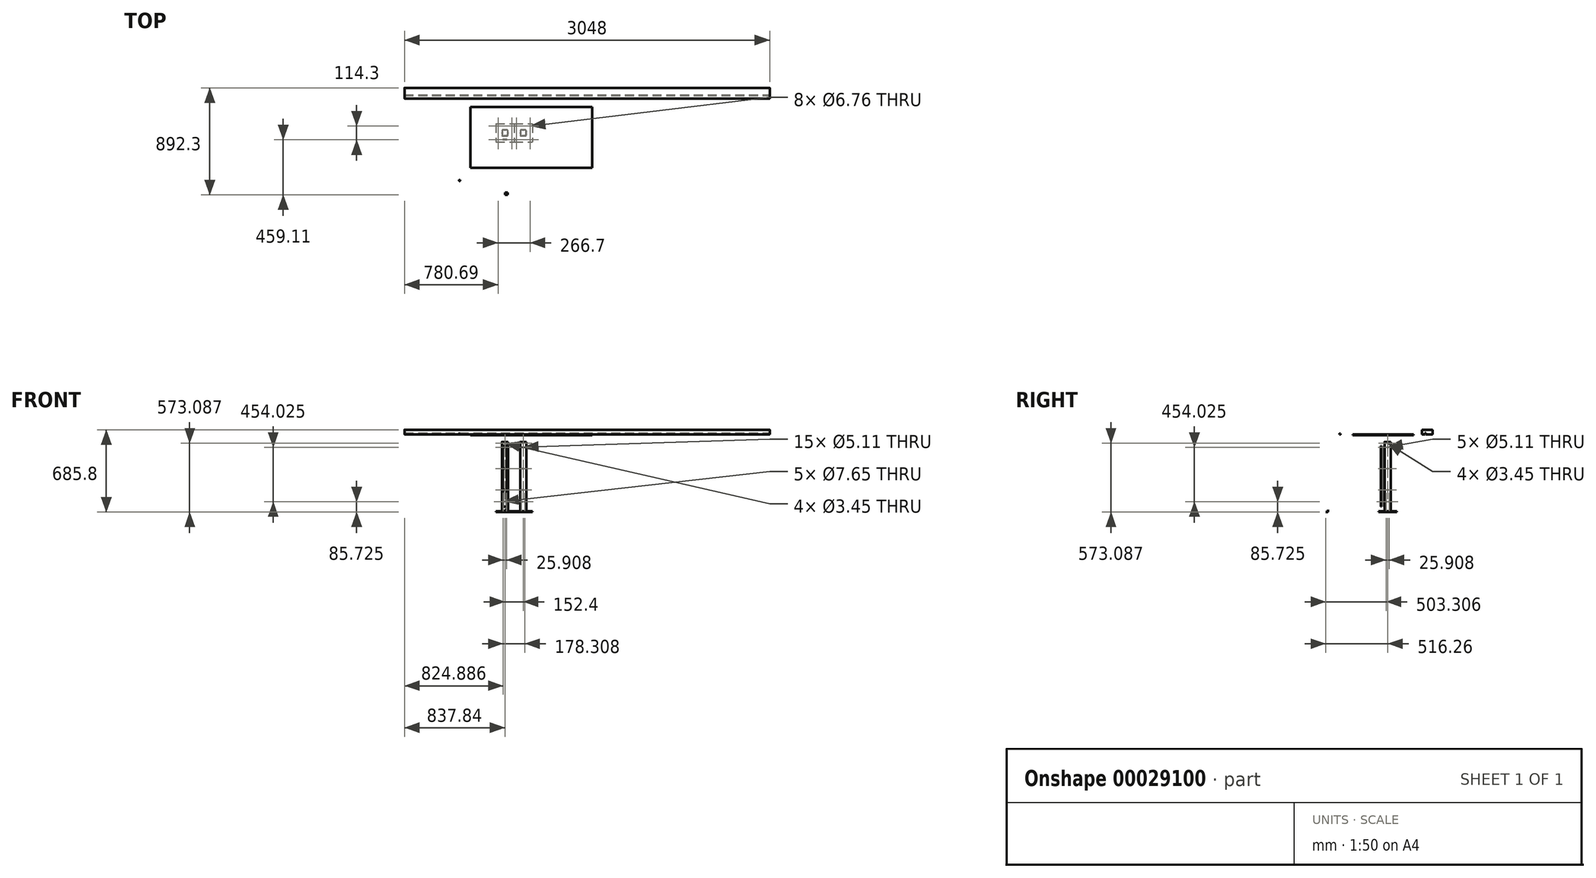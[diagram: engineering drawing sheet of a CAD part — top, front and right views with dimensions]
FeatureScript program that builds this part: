
annotation { "Feature Type Name" : "Feature", "Feature Type Description" : "" }
export const myFeature = defineFeature(function(context is Context, id is Id, definition is map)
    precondition{}
    {
        {
            var Q0;
            Q0=qCreatedBy(makeId("Top.planeOp"),FACE);
            var sketch = newSketch(context, id + "F0", { "sketchPlane" : qUnion([Q0])});
            skLineSegment(sketch, "E0.bottom", {"start": v(-76.2, 76.2) * mm, "end": v(76.2, 76.2) * mm});
            skLineSegment(sketch, "E0.top", {"start": v(-76.2, -76.2) * mm, "end": v(76.2, -76.2) * mm});
            skLineSegment(sketch, "E0.left", {"start": v(-76.2, 76.2) * mm, "end": v(-76.2, -76.2) * mm});
            skLineSegment(sketch, "E0.right", {"start": v(76.2, 76.2) * mm, "end": v(76.2, -76.2) * mm});
            skSolve(sketch);
        }
        {
            var Q0;
            Q0 = qSketchRegion(id + "F0", true);
            extrude(context, id + "F1", {"entities" : qUnion([Q0]), "depth" : 6.35 * mm});
        }
        {
            var Q0;
            Q0=makeQuery(id+"F1.opExtrude","CAP_FACE",FACE,{"disambiguationData":[OSD([sQuery(id+"F0.wireOp",EDGE,"E0.bottom"),sQuery(id+"F0.wireOp",EDGE,"E0.top"),sQuery(id+"F0.wireOp",EDGE,"E0.left"),sQuery(id+"F0.wireOp",EDGE,"E0.right")])],"isStart":false});
            var sketch = newSketch(context, id + "F2", { "sketchPlane" : qUnion([Q0])});
            skLineSegment(sketch, "E1.0", {"start": v(19.3, 25.4) * mm, "end": v(-19.3, 25.4) * mm});
            skLineSegment(sketch, "E1.1", {"start": v(25.4, -19.3) * mm, "end": v(25.4, 19.3) * mm});
            skLineSegment(sketch, "E1.2", {"start": v(-19.3, -25.4) * mm, "end": v(19.3, -25.4) * mm});
            skLineSegment(sketch, "E1.3", {"start": v(-25.4, 19.3) * mm, "end": v(-25.4, -19.3) * mm});
            skLineSegment(sketch, "E2.0", {"start": v(-22.35, 19.3) * mm, "end": v(-22.35, -19.18) * mm});
            skLineSegment(sketch, "E2.1", {"start": v(19.3, 22.35) * mm, "end": v(-19.3, 22.35) * mm});
            skLineSegment(sketch, "E2.2", {"start": v(22.35, -19.3) * mm, "end": v(22.35, 19.3) * mm});
            skLineSegment(sketch, "E2.3", {"start": v(-19.18, -22.35) * mm, "end": v(19.3, -22.35) * mm});
            skPoint(sketch, "E3.visualSharp", {"position": v(-22.35, -22.35) * mm});
            skArc(sketch, "E3.filletArc", {"start": v(-22.35, -19.18) * mm, "mid": v(-21.42, -21.42) * mm, "end": v(-19.18, -22.35) * mm});
            skPoint(sketch, "E4.visualSharp", {"position": v(-25.4, -25.4) * mm});
            skArc(sketch, "E4.filletArc", {"start": v(-25.4, -19.3) * mm, "mid": v(-23.61, -23.61) * mm, "end": v(-19.3, -25.4) * mm});
            skPoint(sketch, "E5.visualSharp", {"position": v(22.35, -22.35) * mm});
            skArc(sketch, "E5.filletArc", {"start": v(19.3, -22.35) * mm, "mid": v(21.46, -21.46) * mm, "end": v(22.35, -19.3) * mm});
            skPoint(sketch, "E6.visualSharp", {"position": v(25.4, -25.4) * mm});
            skArc(sketch, "E6.filletArc", {"start": v(19.3, -25.4) * mm, "mid": v(23.61, -23.61) * mm, "end": v(25.4, -19.3) * mm});
            skPoint(sketch, "E7.visualSharp", {"position": v(22.35, 22.35) * mm});
            skArc(sketch, "E7.filletArc", {"start": v(22.35, 19.3) * mm, "mid": v(21.46, 21.46) * mm, "end": v(19.3, 22.35) * mm});
            skPoint(sketch, "E8.visualSharp", {"position": v(25.4, 25.4) * mm});
            skArc(sketch, "E8.filletArc", {"start": v(25.4, 19.3) * mm, "mid": v(23.61, 23.61) * mm, "end": v(19.3, 25.4) * mm});
            skPoint(sketch, "E9.visualSharp", {"position": v(-22.35, 22.35) * mm});
            skArc(sketch, "E9.filletArc", {"start": v(-19.3, 22.35) * mm, "mid": v(-21.46, 21.46) * mm, "end": v(-22.35, 19.3) * mm});
            skPoint(sketch, "E10.visualSharp", {"position": v(-25.4, 25.4) * mm});
            skArc(sketch, "E10.filletArc", {"start": v(-19.3, 25.4) * mm, "mid": v(-23.61, 23.61) * mm, "end": v(-25.4, 19.3) * mm});
            skSolve(sketch);
        }
        {
            var Q0;
            Q0 = qSketchRegion(id + "F2", true);
            extrude(context, id + "F3", {"entities" : qUnion([Q0]), "operationType" : NewBodyOperationType.ADD, "depth" : 577.85 * mm});
        }
        {
            var Q0;
            Q0=makeQuery(id+"F3.opExtrude","SWEPT_FACE",FACE,{"disambiguationData":[OSD([sQuery(id+"F2.wireOp",EDGE,"E1.2")])]});
            var sketch = newSketch(context, id + "F4", { "sketchPlane" : qUnion([Q0])});
            skPoint(sketch, "E11", {"position": v(12.95, 85.72) * mm});
            skPoint(sketch, "E12", {"position": v(-12.95, 85.72) * mm});
            skPoint(sketch, "E13", {"position": v(0, 539.75) * mm});
            skPoint(sketch, "E14", {"position": v(0, 361.95) * mm});
            skPoint(sketch, "E15", {"position": v(0, 184.15) * mm});
            skPoint(sketch, "E16", {"position": v(0, 573.09) * mm});
            skSolve(sketch);
        }
        {
            var Q0;
            Q0=sQuery(id+"F4.wireOp",VERTEX,"E12");
            var Q1;
            Q1=sQuery(id+"F4.wireOp",VERTEX,"E11");
            var Q2;
            Q2=sQuery(id+"F4.wireOp",VERTEX,"E15");
            var Q3;
            Q3=sQuery(id+"F4.wireOp",VERTEX,"E14");
            var Q4;
            Q4=sQuery(id+"F4.wireOp",VERTEX,"E13");
            var Q5;
            Q5=makeQuery(id+"F1.opExtrude","SWEPT_BODY",BODY,{"disambiguationData":[OSD([sQuery(id+"F0.wireOp",EDGE,"E0.bottom"),sQuery(id+"F0.wireOp",EDGE,"E0.top"),sQuery(id+"F0.wireOp",EDGE,"E0.left"),sQuery(id+"F0.wireOp",EDGE,"E0.right")])]});
            hole(context, id + "F5", {"style" : HoleStyle.SIMPLE, "endStyle" : HoleEndStyle.BLIND, "standardTappedOrClearance" : lookupTablePath({ "standard" : "ANSI", "engagement" : "75%", "pitch" : "20 tpi", "size" : "1/4", "type" : "Tapped" }), "standardBlindInLast" : lookupTablePath({ "standard" : "ANSI", "engagement" : "75%", "pitch" : "20 tpi", "size" : "1/4", "type" : "Tapped" }), "holeDiameter" : 5.1 * mm, "holeDepth" : 12.7 * mm, "locations" : qUnion([Q0, Q1, Q2, Q3, Q4]), "scope" : qUnion([Q5]), "majorDiameter" : 6.35 * mm});
        }
        {
            var Q0;
            Q0=sQuery(id+"F4.wireOp",VERTEX,"E16");
            var Q1;
            Q1=makeQuery(id+"F1.opExtrude","SWEPT_BODY",BODY,{"disambiguationData":[OSD([sQuery(id+"F0.wireOp",EDGE,"E0.bottom"),sQuery(id+"F0.wireOp",EDGE,"E0.top"),sQuery(id+"F0.wireOp",EDGE,"E0.left"),sQuery(id+"F0.wireOp",EDGE,"E0.right")])]});
            hole(context, id + "F6", {"style" : HoleStyle.SIMPLE, "endStyle" : HoleEndStyle.THROUGH, "standardTappedOrClearance" : lookupTablePath({ "standard" : "ANSI", "engagement" : "75%", "pitch" : "32 tpi", "size" : "#8", "type" : "Tapped" }), "standardBlindInLast" : lookupTablePath({ "standard" : "ANSI", "engagement" : "75%", "pitch" : "32 tpi", "size" : "#8", "type" : "Tapped" }), "holeDiameter" : 3.45 * mm, "startFromSketch" : true, "locations" : qUnion([Q0]), "scope" : qUnion([Q1]), "isTappedThrough" : true, "majorDiameter" : 4.17 * mm, "showTappedDepth" : true});
        }
        {
            var Q0;
            {var subQ0=sQuery(id+"F0.wireOp",EDGE,"E0.left");var subQ1=sQuery(id+"F0.wireOp",EDGE,"E0.bottom");var subQ2=sQuery(id+"F0.wireOp",EDGE,"E0.top");var subQ3=sQuery(id+"F0.wireOp",EDGE,"E0.right");Q0=makeQuery(id+"F3.boolean.opBoolean","SPLIT",FACE,{"disambiguationData":[TD([makeQuery(id+"F1.opExtrude","SWEPT_FACE",FACE,{"disambiguationData":[OSD([subQ1])]})])],"derivedFrom":makeQuery(id+"F1.opExtrude","CAP_FACE",FACE,{"disambiguationData":[OSD([subQ1,subQ2,subQ0,subQ3])],"isStart":false})});}
            var sketch = newSketch(context, id + "F7", { "sketchPlane" : qUnion([Q0])});
            skPoint(sketch, "E17", {"position": v(-57.15, 57.15) * mm});
            skPoint(sketch, "E18", {"position": v(-57.15, -57.15) * mm});
            skPoint(sketch, "E19", {"position": v(57.15, -57.15) * mm});
            skPoint(sketch, "E20", {"position": v(57.15, 57.15) * mm});
            skSolve(sketch);
        }
        {
            var Q0;
            Q0=sQuery(id+"F7.wireOp",VERTEX,"E17");
            var Q1;
            Q1=sQuery(id+"F7.wireOp",VERTEX,"E18");
            var Q2;
            Q2=sQuery(id+"F7.wireOp",VERTEX,"E19");
            var Q3;
            Q3=sQuery(id+"F7.wireOp",VERTEX,"E20");
            var Q4;
            Q4=makeQuery(id+"F1.opExtrude","SWEPT_BODY",BODY,{"disambiguationData":[OSD([sQuery(id+"F0.wireOp",EDGE,"E0.bottom"),sQuery(id+"F0.wireOp",EDGE,"E0.top"),sQuery(id+"F0.wireOp",EDGE,"E0.left"),sQuery(id+"F0.wireOp",EDGE,"E0.right")])]});
            hole(context, id + "F8", {"style" : HoleStyle.SIMPLE, "endStyle" : HoleEndStyle.THROUGH, "standardTappedOrClearance" : lookupTablePath({ "standard" : "ANSI", "fit" : "Normal (ASME)", "size" : "1/4", "type" : "Clearance" }), "standardBlindInLast" : lookupTablePath({ "fit" : "Free", "standard" : "ANSI", "size" : "1/4", "type" : "Clearance" }), "holeDiameter" : 6.76 * mm, "locations" : qUnion([Q0, Q1, Q2, Q3]), "scope" : qUnion([Q4]), "isTappedThrough" : true});
        }
        {
            var Q0;
            Q0=makeQuery(id+"F3.opExtrude","SWEPT_FACE",FACE,{"disambiguationData":[OSD([sQuery(id+"F2.wireOp",EDGE,"E1.2")])]});
            var sketch = newSketch(context, id + "F9", { "sketchPlane" : qUnion([Q0])});
            skLineSegment(sketch, "E21.bottom", {"start": v(19.3, 552.45) * mm, "end": v(-19.3, 552.45) * mm});
            skLineSegment(sketch, "E21.top", {"start": v(19.3, 44.45) * mm, "end": v(-19.3, 44.45) * mm});
            skLineSegment(sketch, "E21.left", {"start": v(19.3, 552.45) * mm, "end": v(19.3, 44.45) * mm});
            skLineSegment(sketch, "E21.right", {"start": v(-19.3, 552.45) * mm, "end": v(-19.3, 44.45) * mm});
            skCircle(sketch, "E22.0", {"center": v(-12.95, 85.72) * mm, "radius": 2.55 * mm});
            skCircle(sketch, "E23.0", {"center": v(12.95, 85.72) * mm, "radius": 2.55 * mm});
            skCircle(sketch, "E24.0", {"center": v(0, 184.15) * mm, "radius": 2.55 * mm});
            skCircle(sketch, "E25.0", {"center": v(0, 361.95) * mm, "radius": 2.55 * mm});
            skCircle(sketch, "E26.0", {"center": v(0, 539.75) * mm, "radius": 2.55 * mm});
            skSolve(sketch);
        }
        {
            var Q0;
            Q0 = qSketchRegion(id + "F9", true);
            extrude(context, id + "F10", {"entities" : qUnion([Q0]), "depth" : 3.17 * mm});
        }
        {
            var Q0;
            Q0=makeQuery(id+"F3.opExtrude","SWEPT_FACE",FACE,{"disambiguationData":[OSD([sQuery(id+"F2.wireOp",EDGE,"E1.1")])]});
            var sketch = newSketch(context, id + "F11", { "sketchPlane" : qUnion([Q0])});
            skPoint(sketch, "E27", {"position": v(0, 573.09) * mm});
            skSolve(sketch);
        }
        {
            var Q0;
            Q0=sQuery(id+"F11.wireOp",VERTEX,"E27");
            var Q1;
            Q1=makeQuery(id+"F1.opExtrude","SWEPT_BODY",BODY,{"disambiguationData":[OSD([sQuery(id+"F0.wireOp",EDGE,"E0.bottom"),sQuery(id+"F0.wireOp",EDGE,"E0.top"),sQuery(id+"F0.wireOp",EDGE,"E0.left"),sQuery(id+"F0.wireOp",EDGE,"E0.right")])]});
            hole(context, id + "F12", {"style" : HoleStyle.SIMPLE, "endStyle" : HoleEndStyle.THROUGH, "standardTappedOrClearance" : lookupTablePath({ "standard" : "ANSI", "engagement" : "75%", "pitch" : "32 tpi", "size" : "#8", "type" : "Tapped" }), "standardBlindInLast" : lookupTablePath({ "standard" : "ANSI", "engagement" : "75%", "pitch" : "32 tpi", "size" : "#8", "type" : "Tapped" }), "holeDiameter" : 3.45 * mm, "startFromSketch" : true, "locations" : qUnion([Q0]), "scope" : qUnion([Q1]), "isTappedThrough" : true, "majorDiameter" : 4.17 * mm, "showTappedDepth" : true});
        }
        {
            var Q0;
            Q0=makeQuery(id+"F1.opExtrude","SWEPT_BODY",BODY,{"disambiguationData":[OSD([sQuery(id+"F0.wireOp",EDGE,"E0.bottom"),sQuery(id+"F0.wireOp",EDGE,"E0.top"),sQuery(id+"F0.wireOp",EDGE,"E0.left"),sQuery(id+"F0.wireOp",EDGE,"E0.right")])]});
            transform(context, id + "F13", {"entities" : qUnion([Q0]), "transformType" : TransformType.TRANSLATION_3D, "dx" : 152.4 * mm, "dy" : 0 * mm, "dz" : 0 * mm, "makeCopy" : true});
        }
        {
            var Q0;
            Q0=makeQuery(id+"F13.opPattern","COPY",FACE,{"derivedFrom":makeQuery(id+"F3.opExtrude","SWEPT_FACE",FACE,{"disambiguationData":[OSD([sQuery(id+"F2.wireOp",EDGE,"E1.1")])]}),"instanceName":"1"});
            var sketch = newSketch(context, id + "F14", { "sketchPlane" : qUnion([Q0])});
            skPoint(sketch, "E28", {"position": v(12.95, 85.72) * mm});
            skPoint(sketch, "E29", {"position": v(-12.95, 85.72) * mm});
            skPoint(sketch, "E30", {"position": v(0, 539.75) * mm});
            skPoint(sketch, "E31", {"position": v(0, 361.95) * mm});
            skPoint(sketch, "E32", {"position": v(0, 184.15) * mm});
            skSolve(sketch);
        }
        {
            var Q0;
            Q0=sQuery(id+"F14.wireOp",VERTEX,"E28");
            var Q1;
            Q1=sQuery(id+"F14.wireOp",VERTEX,"E29");
            var Q2;
            Q2=sQuery(id+"F14.wireOp",VERTEX,"E32");
            var Q3;
            Q3=sQuery(id+"F14.wireOp",VERTEX,"E31");
            var Q4;
            Q4=sQuery(id+"F14.wireOp",VERTEX,"E30");
            var Q5;
            Q5=makeQuery(id+"F13.opPattern","COPY",BODY,{"derivedFrom":makeQuery(id+"F1.opExtrude","SWEPT_BODY",BODY,{"disambiguationData":[OSD([sQuery(id+"F0.wireOp",EDGE,"E0.bottom"),sQuery(id+"F0.wireOp",EDGE,"E0.top"),sQuery(id+"F0.wireOp",EDGE,"E0.left"),sQuery(id+"F0.wireOp",EDGE,"E0.right")])]}),"instanceName":"1"});
            hole(context, id + "F15", {"style" : HoleStyle.SIMPLE, "endStyle" : HoleEndStyle.BLIND, "standardTappedOrClearance" : lookupTablePath({ "standard" : "ANSI", "engagement" : "75%", "pitch" : "20 tpi", "size" : "1/4", "type" : "Tapped" }), "standardBlindInLast" : lookupTablePath({ "standard" : "ANSI", "engagement" : "75%", "pitch" : "20 tpi", "size" : "1/4", "type" : "Tapped" }), "holeDiameter" : 5.1 * mm, "holeDepth" : 12.7 * mm, "startFromSketch" : true, "locations" : qUnion([Q0, Q1, Q2, Q3, Q4]), "scope" : qUnion([Q5]), "majorDiameter" : 6.35 * mm});
        }
        {
            var Q0;
            {var subQ0=sQuery(id+"F0.wireOp",EDGE,"E0.left");var subQ1=sQuery(id+"F0.wireOp",EDGE,"E0.bottom");var subQ2=sQuery(id+"F0.wireOp",EDGE,"E0.top");var subQ3=sQuery(id+"F0.wireOp",EDGE,"E0.right");Q0=makeQuery(id+"F13.opPattern","COPY",FACE,{"derivedFrom":makeQuery(id+"F3.boolean.opBoolean","SPLIT",FACE,{"disambiguationData":[TD([makeQuery(id+"F1.opExtrude","SWEPT_FACE",FACE,{"disambiguationData":[OSD([subQ1])]})])],"derivedFrom":makeQuery(id+"F1.opExtrude","CAP_FACE",FACE,{"disambiguationData":[OSD([subQ1,subQ2,subQ0,subQ3])],"isStart":false})}),"instanceName":"1"});}
            cPlane(context, id + "F16", {"entities" : qUnion([Q0]), "cplaneType" : CPlaneType.OFFSET, "offset" : 635 * mm, "width" : 152.4 * mm, "height" : 152.4 * mm});
        }
        {
            var Q0;
            Q0=qCreatedBy(id+"F16.planeOp",FACE);
            var sketch = newSketch(context, id + "F17", { "sketchPlane" : qUnion([Q0])});
            skLineSegment(sketch, "E33.bottom", {"start": v(-286.6, 217.83) * mm, "end": v(729.4, 217.83) * mm});
            skLineSegment(sketch, "E33.top", {"start": v(-286.6, -290.17) * mm, "end": v(729.4, -290.17) * mm});
            skLineSegment(sketch, "E33.left", {"start": v(-286.6, 217.83) * mm, "end": v(-286.6, -290.17) * mm});
            skLineSegment(sketch, "E33.right", {"start": v(729.4, 217.83) * mm, "end": v(729.4, -290.17) * mm});
            skSolve(sketch);
        }
        {
            var Q0;
            Q0 = qSketchRegion(id + "F17", true);
            extrude(context, id + "F18", {"entities" : qUnion([Q0]), "depth" : 6.35 * mm});
        }
        {
            var Q0;
            Q0=makeQuery(id+"F18.opExtrude","CAP_FACE",FACE,{"disambiguationData":[OSD([sQuery(id+"F17.wireOp",EDGE,"E33.bottom"),sQuery(id+"F17.wireOp",EDGE,"E33.top"),sQuery(id+"F17.wireOp",EDGE,"E33.left"),sQuery(id+"F17.wireOp",EDGE,"E33.right")])],"isStart":false});
            var sketch = newSketch(context, id + "F19", { "sketchPlane" : qUnion([Q0])});
            skCircle(sketch, "E34", {"center": v(-378.3, -396.36) * mm, "radius": 3.3 * mm});
            skCircle(sketch, "E35", {"center": v(-378.3, -396.36) * mm, "radius": 4.76 * mm});
            skSolve(sketch);
        }
        {
            var Q0;
            Q0 = qSketchRegion(id + "F19", true);
            extrude(context, id + "F20", {"entities" : qUnion([Q0]), "depth" : 6.35 * mm});
        }
        {
            var Q0;
            Q0=makeQuery(id+"F18.opExtrude","CAP_FACE",FACE,{"disambiguationData":[OSD([sQuery(id+"F17.wireOp",EDGE,"E33.bottom"),sQuery(id+"F17.wireOp",EDGE,"E33.top"),sQuery(id+"F17.wireOp",EDGE,"E33.left"),sQuery(id+"F17.wireOp",EDGE,"E33.right")])],"isStart":false});
            var sketch = newSketch(context, id + "F21", { "sketchPlane" : qUnion([Q0])});
            skLineSegment(sketch, "E36.bottom", {"start": v(-837.84, 376.04) * mm, "end": v(2210.16, 376.04) * mm});
            skLineSegment(sketch, "E36.top", {"start": v(-837.84, 287.14) * mm, "end": v(2210.16, 287.14) * mm});
            skLineSegment(sketch, "E36.left", {"start": v(-837.84, 376.04) * mm, "end": v(-837.84, 287.14) * mm});
            skLineSegment(sketch, "E36.right", {"start": v(2210.16, 376.04) * mm, "end": v(2210.16, 287.14) * mm});
            skSolve(sketch);
        }
        {
            var Q0;
            Q0 = qSketchRegion(id + "F21", true);
            extrude(context, id + "F22", {"entities" : qUnion([Q0]), "depth" : 38.1 * mm});
        }
        {
            var Q0;
            Q0=makeQuery(id+"F22.opExtrude","SWEPT_FACE",FACE,{"disambiguationData":[OSD([sQuery(id+"F21.wireOp",EDGE,"E36.right")])]});
            var sketch = newSketch(context, id + "F23", { "sketchPlane" : qUnion([Q0])});
            skLineSegment(sketch, "E37.bottom", {"start": v(312.54, 647.7) * mm, "end": v(318.9, 647.7) * mm});
            skLineSegment(sketch, "E37.top", {"start": v(312.54, 660.4) * mm, "end": v(318.9, 660.4) * mm});
            skLineSegment(sketch, "E37.left", {"start": v(312.54, 647.7) * mm, "end": v(312.54, 660.4) * mm});
            skLineSegment(sketch, "E37.right", {"start": v(318.9, 647.7) * mm, "end": v(318.9, 660.4) * mm});
            skSolve(sketch);
        }
        {
            var Q0;
            Q0 = qSketchRegion(id + "F23", true);
            extrude(context, id + "F24", {"entities" : qUnion([Q0]), "operationType" : NewBodyOperationType.REMOVE, "endBound" : BoundingType.THROUGH_ALL, "oppositeDirection" : true, "depth" : 25.4 * mm});
        }
        {
            var Q0;
            Q0=makeQuery(id+"F22.opExtrude","CAP_EDGE",EDGE,{"disambiguationData":[OSD([sQuery(id+"F21.wireOp",EDGE,"E36.top")])],"isStart":false});
            var Q1;
            Q1=makeQuery(id+"F22.opExtrude","CAP_EDGE",EDGE,{"disambiguationData":[OSD([sQuery(id+"F21.wireOp",EDGE,"E36.bottom")])],"isStart":false});
            var Q2;
            Q2=makeQuery(id+"F22.opExtrude","CAP_EDGE",EDGE,{"disambiguationData":[OSD([sQuery(id+"F21.wireOp",EDGE,"E36.top")])],"isStart":true});
            var Q3;
            Q3=makeQuery(id+"F22.opExtrude","CAP_EDGE",EDGE,{"disambiguationData":[OSD([sQuery(id+"F21.wireOp",EDGE,"E36.bottom")])],"isStart":true});
            fillet(context, id + "F25", {"entities" : qUnion([Q0, Q1, Q2, Q3]), "radius" : 3.17 * mm, "tangentPropagation" : true, "allowEdgeOverflow" : false});
        }
        {
            var Q0;
            Q0=qCreatedBy(makeId("Right.planeOp"),FACE);
            var sketch = newSketch(context, id + "F26", { "sketchPlane" : qUnion([Q0])});
            skLineSegment(sketch, "E38.bottom", {"start": v(-516.26, 1.52) * mm, "end": v(-500.32, 1.52) * mm});
            skLineSegment(sketch, "E38.top", {"start": v(-516.26, 0) * mm, "end": v(-498.8, 0) * mm});
            skLineSegment(sketch, "E38.left", {"start": v(-516.26, 1.52) * mm, "end": v(-516.26, 0) * mm});
            skLineSegment(sketch, "E39.bottom", {"start": v(-498.73, 19.05) * mm, "end": v(-497.2, 19.05) * mm});
            skLineSegment(sketch, "E39.left", {"start": v(-498.73, 19.05) * mm, "end": v(-498.73, 3.11) * mm});
            skLineSegment(sketch, "E39.right", {"start": v(-497.2, 19.05) * mm, "end": v(-497.2, 1.59) * mm});
            skPoint(sketch, "E40.visualSharp", {"position": v(-498.73, 1.52) * mm});
            skArc(sketch, "E40.filletArc", {"start": v(-500.32, 1.52) * mm, "mid": v(-499.2, 1.99) * mm, "end": v(-498.73, 3.11) * mm});
            skPoint(sketch, "E41.visualSharp", {"position": v(-497.2, 0) * mm});
            skArc(sketch, "E41.filletArc", {"start": v(-498.8, 0) * mm, "mid": v(-497.67, 0.46) * mm, "end": v(-497.2, 1.59) * mm});
            skSolve(sketch);
        }
        {
            var Q0;
            Q0 = qSketchRegion(id + "F26", true);
            extrude(context, id + "F27", {"entities" : qUnion([Q0]), "depth" : 22.22 * mm});
        }
        {
            var Q0;
            Q0=makeQuery(id+"F27.opExtrude","SWEPT_FACE",FACE,{"disambiguationData":[OSD([sQuery(id+"F26.wireOp",EDGE,"E38.bottom")])]});
            var sketch = newSketch(context, id + "F28", { "sketchPlane" : qUnion([Q0])});
            skLineSegment(sketch, "E42", {"start": v(11.11, -505.01) * mm, "end": v(11.11, -512.67) * mm});
            skArc(sketch, "E43.0.startCap", {"start": v(9.08, -505.01) * mm, "mid": v(11.11, -502.98) * mm, "end": v(13.14, -505.01) * mm});
            skArc(sketch, "E43.0.endCap", {"start": v(13.14, -512.67) * mm, "mid": v(11.11, -514.7) * mm, "end": v(9.08, -512.67) * mm});
            skLineSegment(sketch, "E43.0.left", {"start": v(13.14, -505.01) * mm, "end": v(13.14, -512.67) * mm});
            skLineSegment(sketch, "E43.0.right", {"start": v(9.08, -505.01) * mm, "end": v(9.08, -512.67) * mm});
            skSolve(sketch);
        }
        {
            var Q0;
            Q0 = qSketchRegion(id + "F28", true);
            extrude(context, id + "F29", {"entities" : qUnion([Q0]), "operationType" : NewBodyOperationType.REMOVE, "endBound" : BoundingType.THROUGH_ALL, "oppositeDirection" : true, "depth" : 25.4 * mm});
        }
        {
            var Q0;
            Q0=makeQuery(id+"F27.opExtrude","SWEPT_FACE",FACE,{"disambiguationData":[OSD([sQuery(id+"F26.wireOp",EDGE,"E39.left")])]});
            var sketch = newSketch(context, id + "F30", { "sketchPlane" : qUnion([Q0])});
            skPoint(sketch, "E44", {"position": v(11.11, 9.45) * mm});
            skSolve(sketch);
        }
        {
            var Q0;
            Q0=sQuery(id+"F30.wireOp",VERTEX,"E44");
            var Q1;
            Q1=makeQuery(id+"F27.opExtrude","SWEPT_BODY",BODY,{"disambiguationData":[OSD([sQuery(id+"F26.wireOp",EDGE,"E38.bottom"),sQuery(id+"F26.wireOp",EDGE,"E38.top"),sQuery(id+"F26.wireOp",EDGE,"E38.left"),sQuery(id+"F26.wireOp",EDGE,"E39.bottom"),sQuery(id+"F26.wireOp",EDGE,"E39.left"),sQuery(id+"F26.wireOp",EDGE,"E39.right"),sQuery(id+"F26.wireOp",EDGE,"E40.filletArc"),sQuery(id+"F26.wireOp",EDGE,"E41.filletArc")])]});
            hole(context, id + "F31", {"style" : HoleStyle.SIMPLE, "endStyle" : HoleEndStyle.THROUGH, "standardTappedOrClearance" : lookupTablePath({ "standard" : "ANSI", "fit" : "Normal (ASME)", "size" : "#8", "type" : "Clearance" }), "standardBlindInLast" : lookupTablePath({ "fit" : "Free", "standard" : "ANSI", "size" : "#8", "type" : "Clearance" }), "holeDiameter" : 4.5 * mm, "startFromSketch" : true, "locations" : qUnion([Q0]), "scope" : qUnion([Q1]), "isTappedThrough" : true});
        }
        {
            var Q0;
            Q0=makeQuery(id+"F10.opExtrude","CAP_FACE",FACE,{"disambiguationData":[OSD([sQuery(id+"F9.wireOp",EDGE,"E21.bottom"),sQuery(id+"F9.wireOp",EDGE,"E21.top"),sQuery(id+"F9.wireOp",EDGE,"E21.left"),sQuery(id+"F9.wireOp",EDGE,"E21.right"),sQuery(id+"F9.wireOp",EDGE,"E22.0"),sQuery(id+"F9.wireOp",EDGE,"E23.0"),sQuery(id+"F9.wireOp",EDGE,"E24.0"),sQuery(id+"F9.wireOp",EDGE,"E25.0"),sQuery(id+"F9.wireOp",EDGE,"E26.0")])],"isStart":false});
            cPlane(context, id + "F32", {"entities" : qUnion([Q0]), "cplaneType" : CPlaneType.OFFSET, "offset" : 25.4 * mm, "width" : 152.4 * mm, "height" : 152.4 * mm});
        }
        {
            var Q0;
            Q0=qCreatedBy(id+"F32.planeOp",FACE);
            var sketch = newSketch(context, id + "F33", { "sketchPlane" : qUnion([Q0])});
            skLineSegment(sketch, "E45.0", {"start": v(18.03, 45.72) * mm, "end": v(18.03, 551.18) * mm});
            skLineSegment(sketch, "E45.1", {"start": v(-18.03, 45.72) * mm, "end": v(18.03, 45.72) * mm});
            skLineSegment(sketch, "E45.2", {"start": v(-18.03, 551.18) * mm, "end": v(-18.03, 45.72) * mm});
            skLineSegment(sketch, "E45.3", {"start": v(18.03, 551.18) * mm, "end": v(-18.03, 551.18) * mm});
            skCircle(sketch, "E46.0", {"center": v(0, 184.15) * mm, "radius": 3.82 * mm});
            skCircle(sketch, "E47.0", {"center": v(0, 361.95) * mm, "radius": 3.82 * mm});
            skCircle(sketch, "E48.0", {"center": v(-12.95, 85.72) * mm, "radius": 3.82 * mm});
            skCircle(sketch, "E49.0", {"center": v(12.95, 85.72) * mm, "radius": 3.82 * mm});
            skCircle(sketch, "E50.0", {"center": v(0, 539.75) * mm, "radius": 3.82 * mm});
            skSolve(sketch);
        }
        {
            var Q0;
            Q0 = qSketchRegion(id + "F33", true);
            extrude(context, id + "F34", {"entities" : qUnion([Q0]), "depth" : 1.59 * mm});
        }
    });
